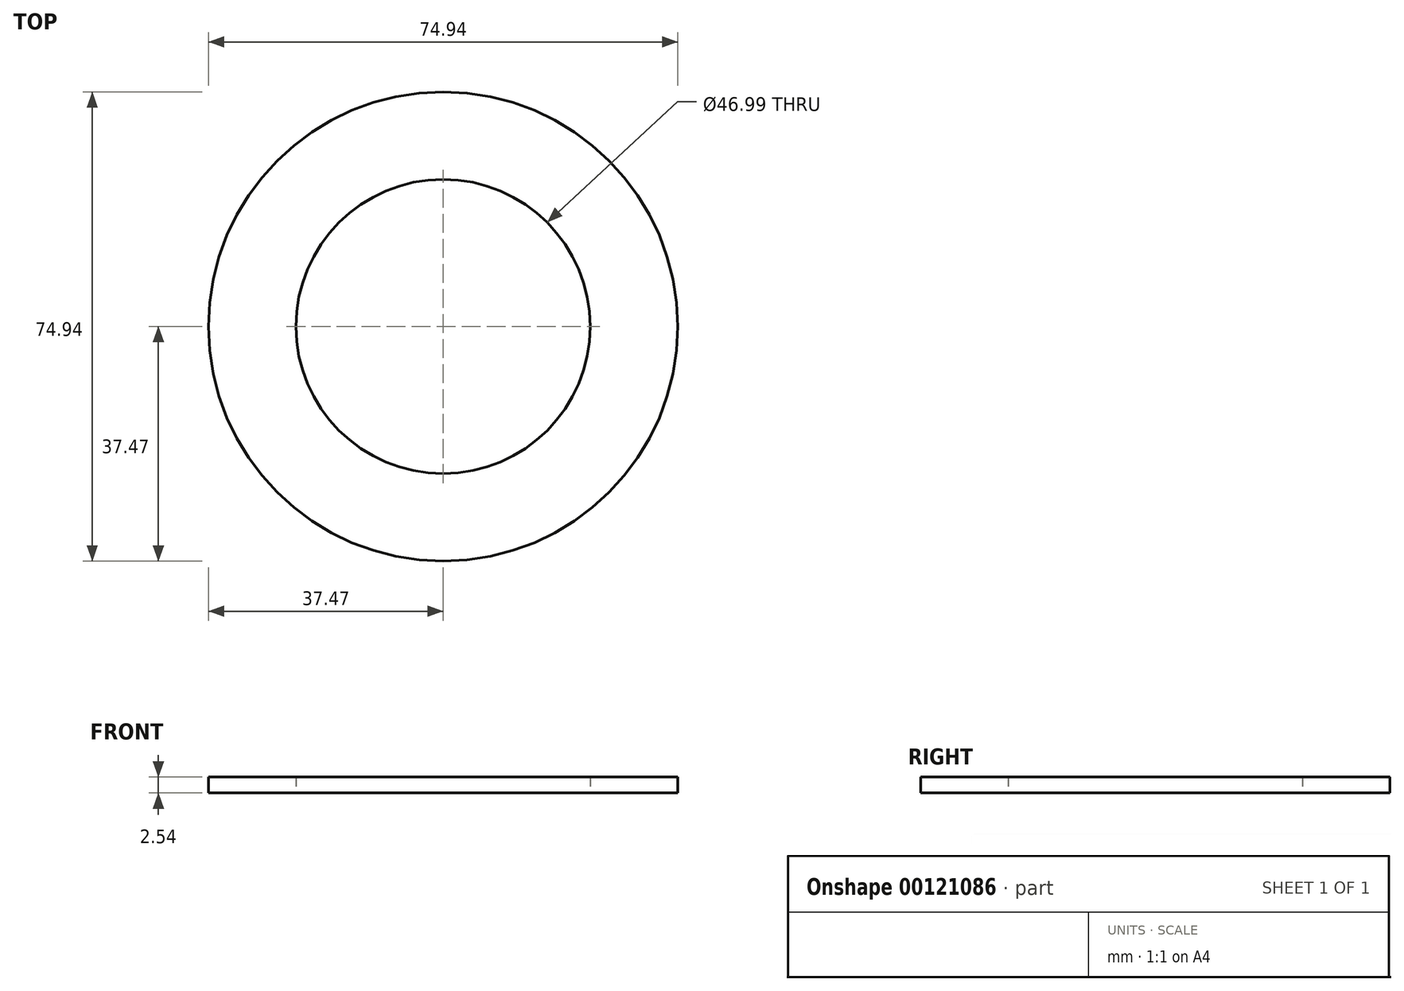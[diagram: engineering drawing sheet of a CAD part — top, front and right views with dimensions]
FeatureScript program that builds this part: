
annotation { "Feature Type Name" : "Feature", "Feature Type Description" : "" }
export const myFeature = defineFeature(function(context is Context, id is Id, definition is map)
    precondition{}
    {
        {
            var Q0;
            Q0=qCreatedBy(makeId("Top.planeOp"),FACE);
            var sketch = newSketch(context, id + "F0", { "sketchPlane" : qUnion([Q0])});
            skCircle(sketch, "E0", {"center": v(0, 0) * mm, "radius": 37.47 * mm});
            skCircle(sketch, "E1", {"center": v(0, 0) * mm, "radius": 23.5 * mm});
            skSolve(sketch);
        }
        {
            var Q0;
            Q0 = qSketchRegion(id + "F0", true);
            extrude(context, id + "F1", {"entities" : qUnion([Q0]), "depth" : 2.54 * mm});
        }
    });
